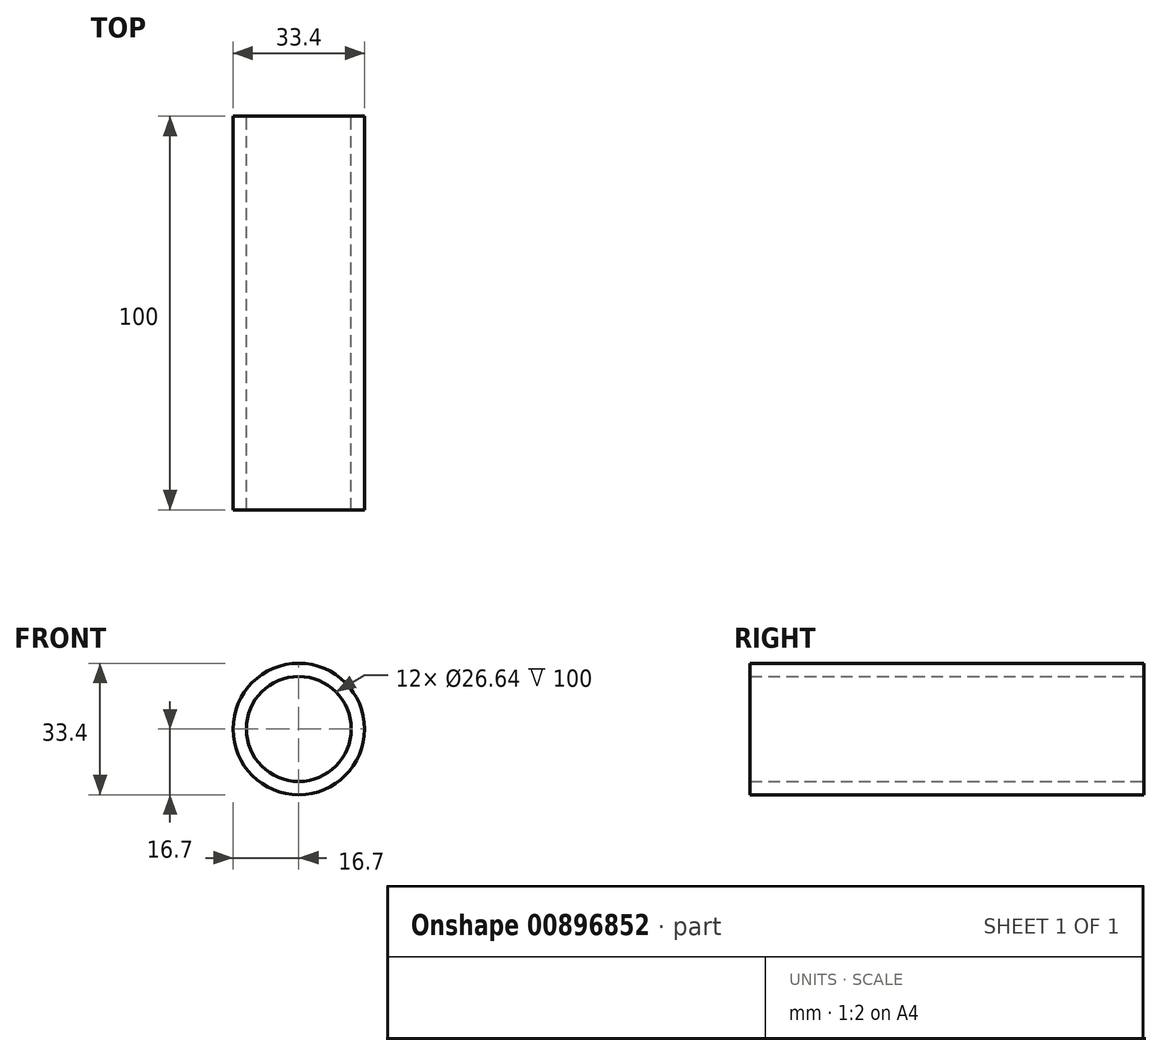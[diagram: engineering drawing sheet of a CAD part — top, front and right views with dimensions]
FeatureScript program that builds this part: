
annotation { "Feature Type Name" : "Feature", "Feature Type Description" : "" }
export const myFeature = defineFeature(function(context is Context, id is Id, definition is map)
    precondition{}
    {
        {
            var Q0;
            Q0=qCreatedBy(makeId("Front.planeOp"),FACE);
            var sketch = newSketch(context, id + "F0", { "sketchPlane" : qUnion([Q0])});
            skCircle(sketch, "E0", {"center": v(0, 0) * mm, "radius": 16.7 * mm});
            skCircle(sketch, "E1", {"center": v(0, 0) * mm, "radius": 13.32 * mm});
            skSolve(sketch);
        }
        {
            var Q0;
            Q0=makeQuery(id+"F0.imprint","IMPRINT",FACE,{"disambiguationData":[TD([[makeQuery(id+"F0.imprint","IMPRINT",EDGE,{"derivedFrom":sQuery(id+"F0.wireOp",EDGE,"E0")}),1.0]])]});
            extrude(context, id + "F1", {"entities" : qUnion([Q0]), "depth" : 100 * mm, "offsetDistance" : 25.4 * mm});
        }
    });
